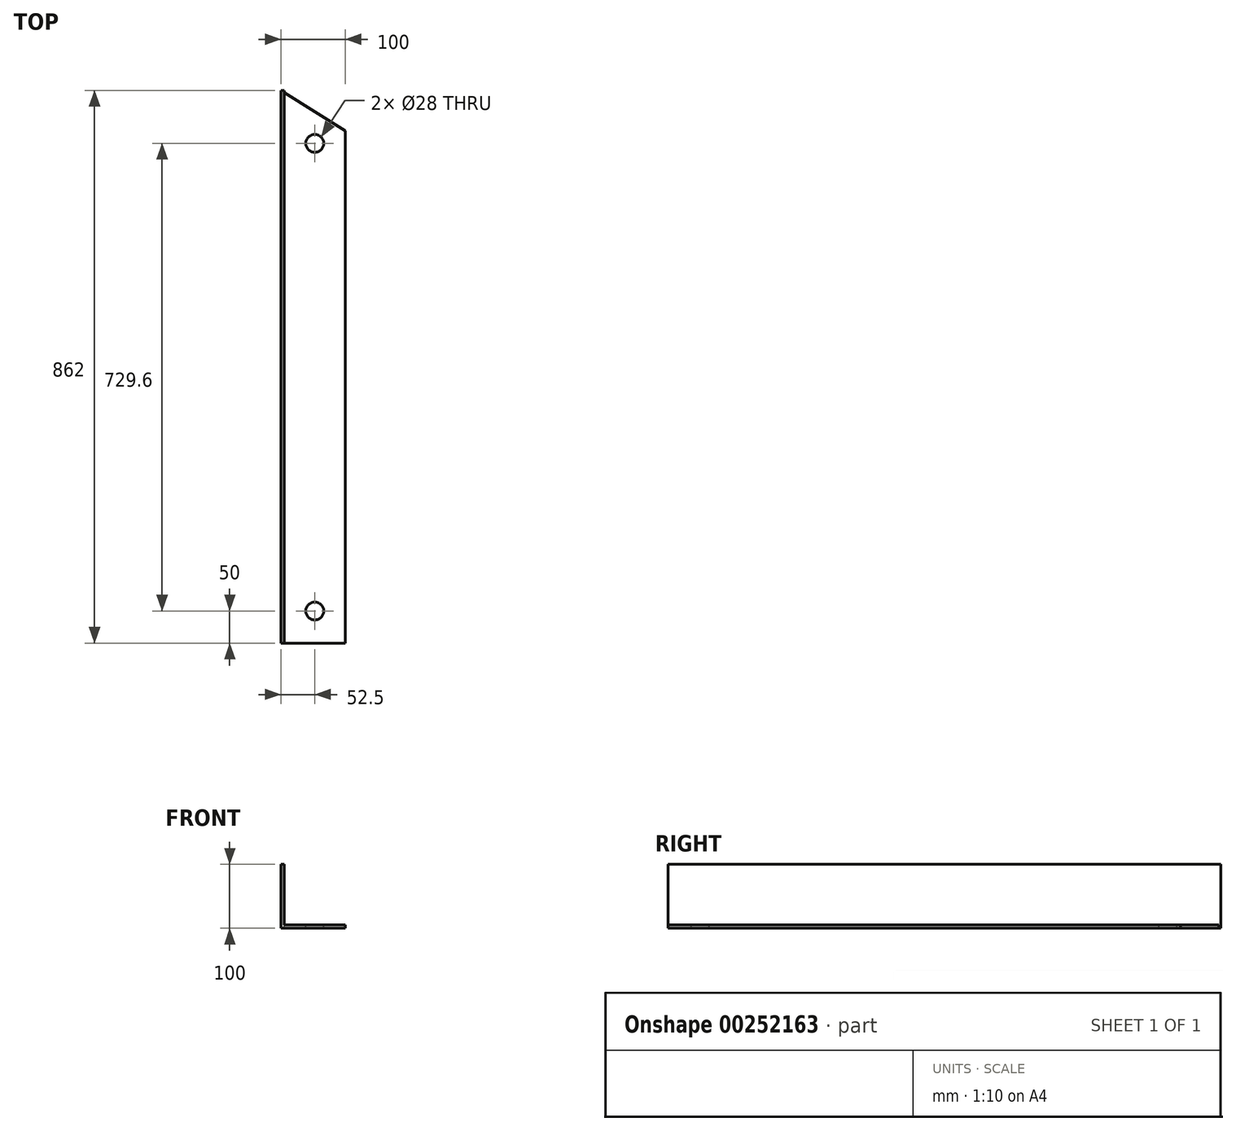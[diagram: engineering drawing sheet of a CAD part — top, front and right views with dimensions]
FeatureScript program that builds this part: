
annotation { "Feature Type Name" : "Feature", "Feature Type Description" : "" }
export const myFeature = defineFeature(function(context is Context, id is Id, definition is map)
    precondition{}
    {
        {
            var Q0;
            Q0=qCreatedBy(makeId("Front.planeOp"),FACE);
            var sketch = newSketch(context, id + "F0", { "sketchPlane" : qUnion([Q0])});
            skLineSegment(sketch, "E0", {"start": v(0, 0) * mm, "end": v(0, 100) * mm});
            skLineSegment(sketch, "E1", {"start": v(0, 100) * mm, "end": v(5, 100) * mm});
            skLineSegment(sketch, "E2", {"start": v(5, 100) * mm, "end": v(5, 5) * mm});
            skLineSegment(sketch, "E3", {"start": v(5, 5) * mm, "end": v(100, 5) * mm});
            skLineSegment(sketch, "E4", {"start": v(100, 5) * mm, "end": v(100, 0) * mm});
            skLineSegment(sketch, "E5", {"start": v(100, 0) * mm, "end": v(0, 0) * mm});
            skSolve(sketch);
        }
        {
            var Q0;
            Q0=makeQuery(id+"F0.imprint","IMPRINT",FACE,{"disambiguationData":[TD([[makeQuery(id+"F0.imprint","IMPRINT",EDGE,{"derivedFrom":sQuery(id+"F0.wireOp",EDGE,"E0")}),-1.0]])]});
            extrude(context, id + "F1", {"entities" : qUnion([Q0]), "depth" : 862 * mm});
        }
        {
            var Q0;
            Q0=makeQuery(id+"F1.opExtrude","SWEPT_FACE",FACE,{"disambiguationData":[OSD([sQuery(id+"F0.wireOp",EDGE,"E3")])]});
            var sketch = newSketch(context, id + "F2", { "sketchPlane" : qUnion([Q0])});
            skCircle(sketch, "E6", {"center": v(52.5, -812) * mm, "radius": 14 * mm});
            skCircle(sketch, "E7", {"center": v(52.5, -82.4) * mm, "radius": 14 * mm});
            skSolve(sketch);
        }
        {
            var Q0;
            Q0=makeQuery(id+"F2.imprint","IMPRINT",FACE,{"disambiguationData":[TD([[makeQuery(id+"F2.imprint","IMPRINT",EDGE,{"derivedFrom":sQuery(id+"F2.wireOp",EDGE,"E7")}),1.0]])]});
            var Q1;
            Q1=makeQuery(id+"F2.imprint","IMPRINT",FACE,{"disambiguationData":[TD([[makeQuery(id+"F2.imprint","IMPRINT",EDGE,{"derivedFrom":sQuery(id+"F2.wireOp",EDGE,"E6")}),1.0]])]});
            var Q2;
            Q2=makeQuery(id+"F1.opExtrude","SWEPT_FACE",FACE,{"disambiguationData":[OSD([sQuery(id+"F0.wireOp",EDGE,"E5")])]});
            extrude(context, id + "F3", {"entities" : qUnion([Q0, Q1]), "operationType" : NewBodyOperationType.REMOVE, "endBound" : BoundingType.UP_TO_SURFACE, "oppositeDirection" : true, "endBoundEntityFace" : qUnion([Q2]), "depth" : 25 * mm});
        }
        {
            var Q0;
            Q0=makeQuery(id+"F2.imprint","IMPRINT",FACE,{"disambiguationData":[TD([[makeQuery(id+"F2.imprint","IMPRINT",EDGE,{"derivedFrom":sQuery(id+"F2.wireOp",EDGE,"E6")}),-1.0]])]});
            var sketch = newSketch(context, id + "F4", { "sketchPlane" : qUnion([Q0])});
            skLineSegment(sketch, "E8", {"start": v(100, -62.49) * mm, "end": v(0, 0) * mm});
            skSolve(sketch);
        }
        {
            var Q0;
            {var subQ1=sQuery(id+"F0.wireOp",EDGE,"E3");var subQ6=makeQuery(id+"F2.imprint","IMPRINT",EDGE,{"derivedFrom":makeQuery(id+"F1.opExtrude","CAP_EDGE",EDGE,{"disambiguationData":[OSD([subQ1])],"isStart":true})});Q0=makeQuery(id+"F4.imprint","IMPRINT",FACE,{"disambiguationData":[TD([[makeQuery(id+"F4.imprint","IMPRINT",EDGE,{"derivedFrom":subQ6}),-1.0]])]});}
            extrude(context, id + "F5", {"entities" : qUnion([Q0]), "operationType" : NewBodyOperationType.REMOVE, "oppositeDirection" : true, "depth" : 5 * mm});
        }
    });
